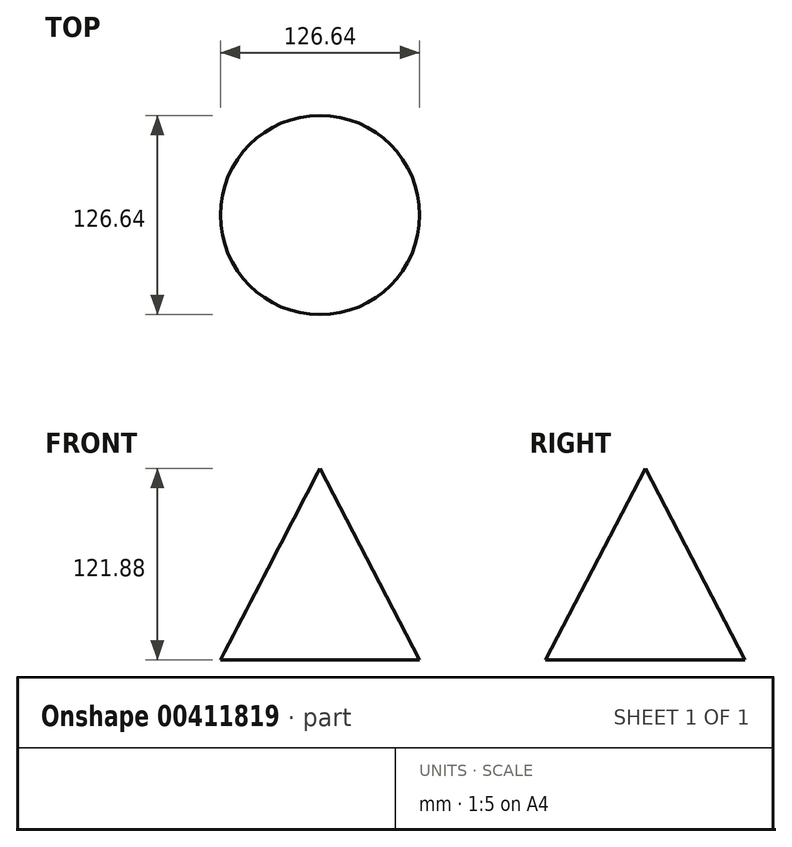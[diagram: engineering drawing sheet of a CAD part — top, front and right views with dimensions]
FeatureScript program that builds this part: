
annotation { "Feature Type Name" : "Feature", "Feature Type Description" : "" }
export const myFeature = defineFeature(function(context is Context, id is Id, definition is map)
    precondition{}
    {
        {
            var Q0;
            Q0=qCreatedBy(makeId("Front.planeOp"),FACE);
            var sketch = newSketch(context, id + "F0", { "sketchPlane" : qUnion([Q0])});
            skLineSegment(sketch, "E0", {"start": v(0, -60.87) * mm, "end": v(0, 61.01) * mm});
            skLineSegment(sketch, "E1", {"start": v(0, 61.01) * mm, "end": v(63.32, -60.87) * mm});
            skLineSegment(sketch, "E2", {"start": v(63.32, -60.87) * mm, "end": v(0, -60.87) * mm});
            skSolve(sketch);
        }
        {
            var Q0;
            Q0=makeQuery(id+"F0.imprint","IMPRINT",FACE,{"disambiguationData":[TD([[makeQuery(id+"F0.imprint","IMPRINT",EDGE,{"derivedFrom":sQuery(id+"F0.wireOp",EDGE,"E0")}),-1.0]])]});
            var Q1;
            Q1=sQuery(id+"F0.wireOp",EDGE,"E0");
            revolve(context, id + "F1", {"entities" : qUnion([Q0]), "axis" : qUnion([Q1]), "revolveType" : RevolveType.FULL});
        }
    });
